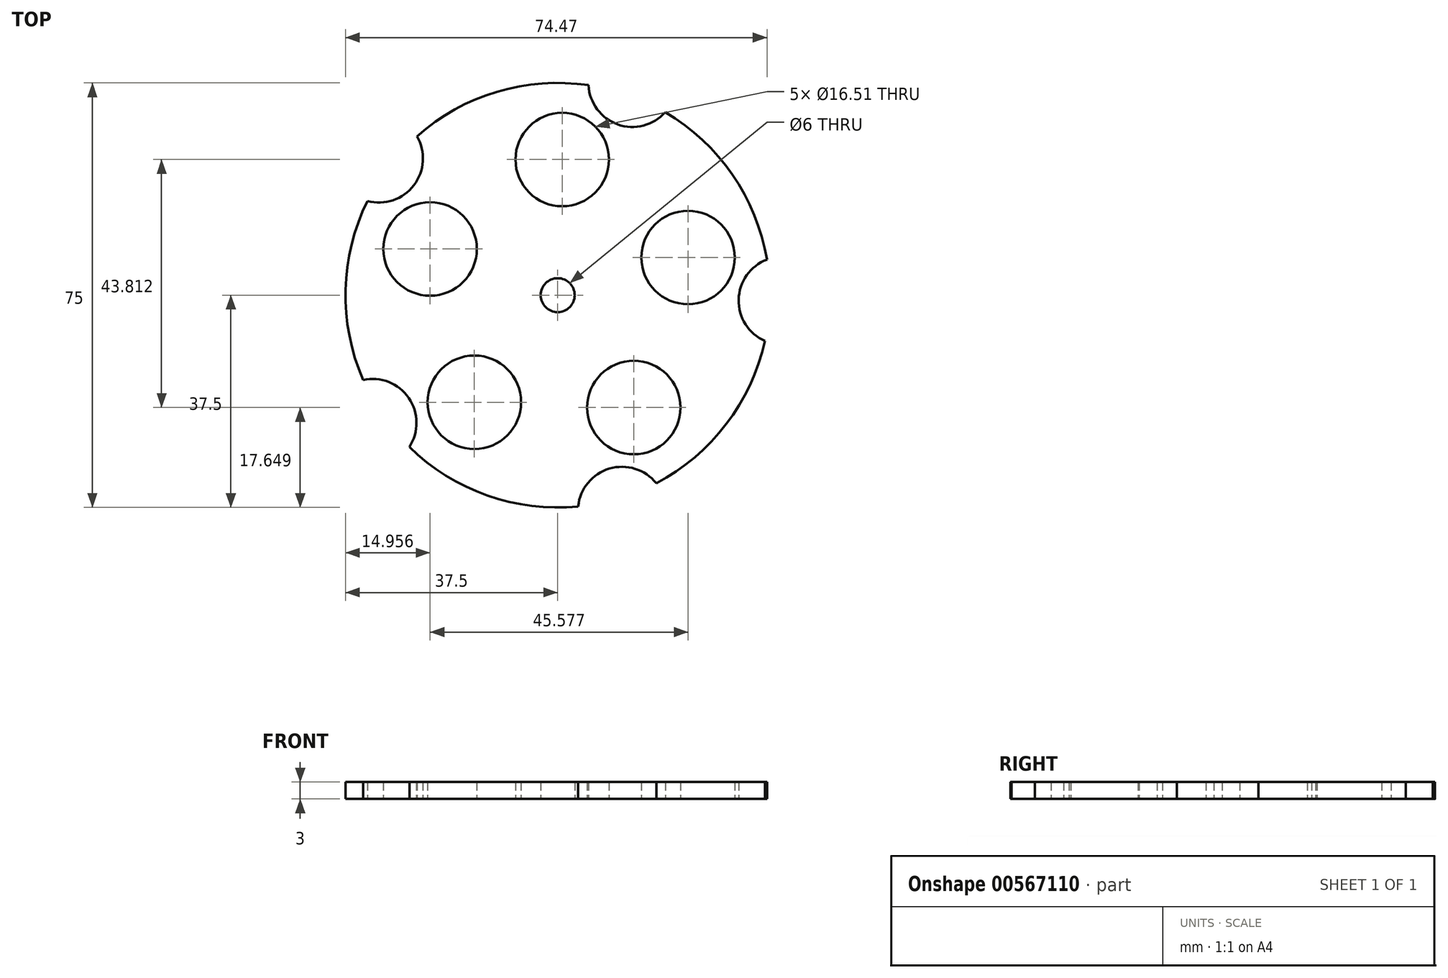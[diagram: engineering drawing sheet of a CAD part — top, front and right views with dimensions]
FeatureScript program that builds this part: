
annotation { "Feature Type Name" : "Feature", "Feature Type Description" : "" }
export const myFeature = defineFeature(function(context is Context, id is Id, definition is map)
    precondition{}
    {
        {
            var Q0;
            Q0=qCreatedBy(makeId("Top.planeOp"),FACE);
            var sketch = newSketch(context, id + "F0", { "sketchPlane" : qUnion([Q0])});
            skLineSegment(sketch, "E0.bottom", {"start": v(0, 0) * mm, "end": v(75, 0) * mm, "construction": true});
            skLineSegment(sketch, "E0.top", {"start": v(0, 75) * mm, "end": v(75, 75) * mm, "construction": true});
            skLineSegment(sketch, "E0.left", {"start": v(0, 0) * mm, "end": v(0, 75) * mm, "construction": true});
            skLineSegment(sketch, "E0.right", {"start": v(75, 0) * mm, "end": v(75, 75) * mm, "construction": true});
            skLineSegment(sketch, "E1", {"start": v(0, 75) * mm, "end": v(75, 0) * mm, "construction": true});
            skCircle(sketch, "E2", {"center": v(37.5, 37.5) * mm, "radius": 3 * mm});
            skCircle(sketch, "E3", {"center": v(37.5, 37.5) * mm, "radius": 37.5 * mm});
            skCircle(sketch, "E4", {"center": v(38.3, 61.46) * mm, "radius": 8.25 * mm});
            skCircle(sketch, "E5", {"center": v(50.7, 75) * mm, "radius": 7.78 * mm});
            skCircle(sketch, "E6.1.0", {"center": v(5.92, 61.65) * mm, "radius": 7.78 * mm});
            skCircle(sketch, "E6.1.1", {"center": v(14.96, 45.66) * mm, "radius": 8.25 * mm});
            skCircle(sketch, "E6.2.0", {"center": v(4.77, 14.92) * mm, "radius": 7.78 * mm});
            skCircle(sketch, "E6.2.1", {"center": v(22.77, 18.58) * mm, "radius": 8.25 * mm});
            skCircle(sketch, "E6.3.0", {"center": v(48.86, -0.6) * mm, "radius": 7.78 * mm});
            skCircle(sketch, "E6.3.1", {"center": v(50.94, 17.65) * mm, "radius": 8.25 * mm});
            skCircle(sketch, "E6.4.0", {"center": v(77.25, 36.53) * mm, "radius": 7.78 * mm});
            skCircle(sketch, "E6.4.1", {"center": v(60.53, 44.15) * mm, "radius": 8.25 * mm});
            skSolve(sketch);
        }
        {
            var Q0;
            Q0=makeQuery(id+"F0.imprint","IMPRINT",FACE,{"disambiguationData":[TD([[makeQuery(id+"F0.imprint","IMPRINT",EDGE,{"derivedFrom":sQuery(id+"F0.wireOp",EDGE,"E2")}),-1.0]])]});
            extrude(context, id + "F1", {"entities" : qUnion([Q0]), "depth" : 3 * mm, "offsetDistance" : 25 * mm});
        }
    });
